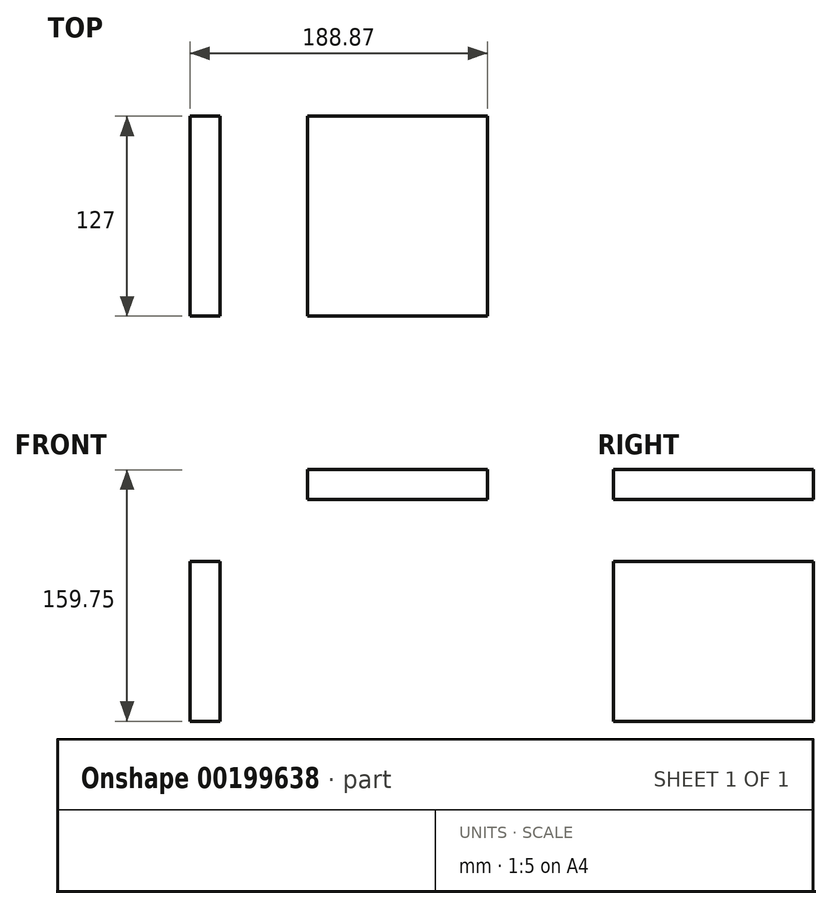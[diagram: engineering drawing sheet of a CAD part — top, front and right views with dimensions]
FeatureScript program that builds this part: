
annotation { "Feature Type Name" : "Feature", "Feature Type Description" : "" }
export const myFeature = defineFeature(function(context is Context, id is Id, definition is map)
    precondition{}
    {
        {
            var Q0;
            Q0=qCreatedBy(makeId("Front.planeOp"),FACE);
            var sketch = newSketch(context, id + "F0", { "sketchPlane" : qUnion([Q0])});
            skLineSegment(sketch, "E0.bottom", {"start": v(146.5, 8.56) * mm, "end": v(165.55, 8.56) * mm});
            skLineSegment(sketch, "E0.top", {"start": v(146.5, -93.04) * mm, "end": v(165.55, -93.04) * mm});
            skLineSegment(sketch, "E0.left", {"start": v(146.5, 8.56) * mm, "end": v(146.5, -93.04) * mm});
            skLineSegment(sketch, "E0.right", {"start": v(165.55, 8.56) * mm, "end": v(165.55, -93.04) * mm});
            skSolve(sketch);
        }
        {
            var Q0;
            Q0=makeQuery(id+"F0.imprint","IMPRINT",FACE,{"disambiguationData":[TD([[makeQuery(id+"F0.imprint","IMPRINT",EDGE,{"derivedFrom":sQuery(id+"F0.wireOp",EDGE,"E0.bottom")}),-1.0]])]});
            extrude(context, id + "F1", {"entities" : qUnion([Q0]), "endBound" : BoundingType.SYMMETRIC, "depth" : 127 * mm});
        }
        {
            var Q0;
            Q0=qCreatedBy(makeId("Front.planeOp"),FACE);
            var sketch = newSketch(context, id + "F2", { "sketchPlane" : qUnion([Q0])});
            skLineSegment(sketch, "E1.bottom", {"start": v(221.07, 66.71) * mm, "end": v(335.37, 66.71) * mm});
            skLineSegment(sketch, "E1.top", {"start": v(221.07, 47.66) * mm, "end": v(335.37, 47.66) * mm});
            skLineSegment(sketch, "E1.left", {"start": v(221.07, 66.71) * mm, "end": v(221.07, 47.66) * mm});
            skLineSegment(sketch, "E1.right", {"start": v(335.37, 66.71) * mm, "end": v(335.37, 47.66) * mm});
            skSolve(sketch);
        }
        {
            var Q0;
            Q0=makeQuery(id+"F2.imprint","IMPRINT",FACE,{"disambiguationData":[TD([[makeQuery(id+"F2.imprint","IMPRINT",EDGE,{"derivedFrom":sQuery(id+"F2.wireOp",EDGE,"E1.bottom")}),-1.0]])]});
            extrude(context, id + "F3", {"entities" : qUnion([Q0]), "endBound" : BoundingType.SYMMETRIC, "depth" : 127 * mm});
        }
    });
